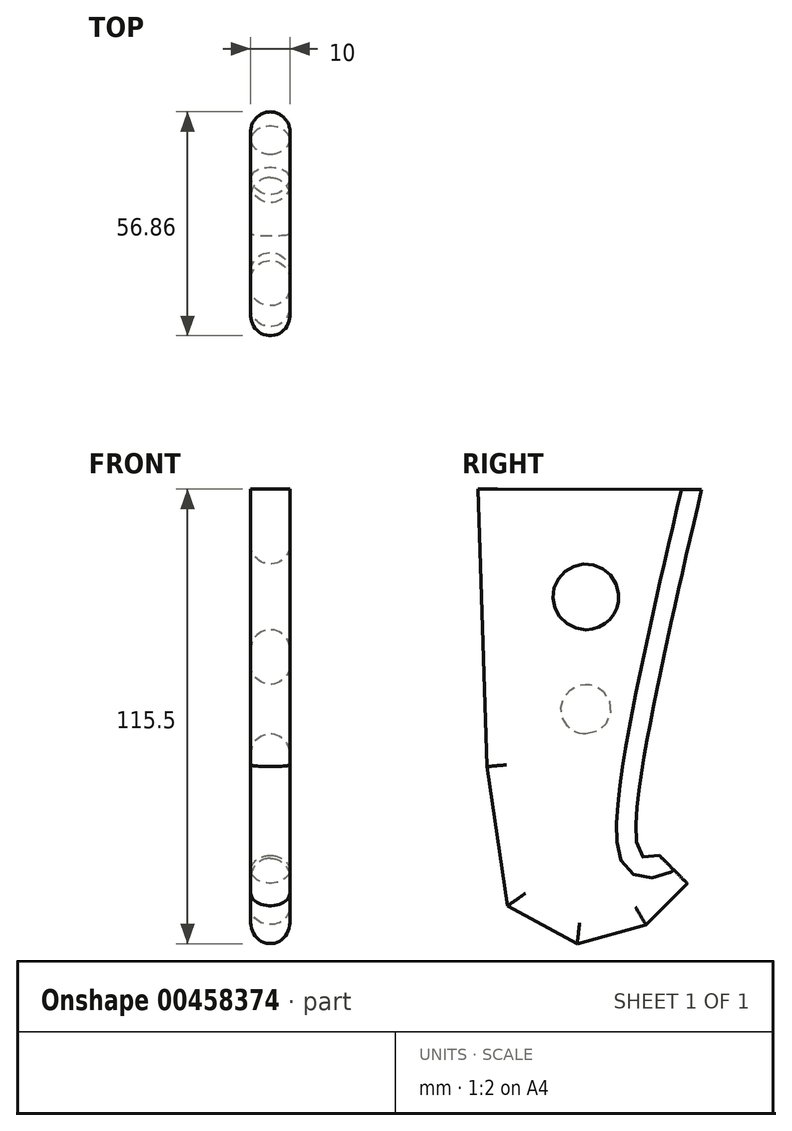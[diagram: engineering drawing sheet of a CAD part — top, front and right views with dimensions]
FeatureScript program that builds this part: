
annotation { "Feature Type Name" : "Feature", "Feature Type Description" : "" }
export const myFeature = defineFeature(function(context is Context, id is Id, definition is map)
    precondition{}
    {
        {
            var Q0;
            Q0=qCreatedBy(makeId("Top.planeOp"),FACE);
            var sketch = newSketch(context, id + "F0", { "sketchPlane" : qUnion([Q0])});
            skLineSegment(sketch, "E0.bottom", {"start": v(50, 50) * mm, "end": v(-50, 50) * mm});
            skLineSegment(sketch, "E0.top", {"start": v(50, -50) * mm, "end": v(-50, -50) * mm});
            skLineSegment(sketch, "E0.left", {"start": v(50, 50) * mm, "end": v(50, -50) * mm});
            skLineSegment(sketch, "E0.right", {"start": v(-50, 50) * mm, "end": v(-50, -50) * mm});
            skPoint(sketch, "E0.middle", {"position": v(0, 0) * mm});
            skSolve(sketch);
        }
        {
            var Q0;
            Q0=qCreatedBy(makeId("Right.planeOp"),FACE);
            var sketch = newSketch(context, id + "F1", { "sketchPlane" : qUnion([Q0])});
            skLineSegment(sketch, "E1", {"start": v(32.93, -92.93) * mm, "end": v(40, -100) * mm});
            skLineSegment(sketch, "E2", {"start": v(40, -100) * mm, "end": v(50, -100) * mm});
            skLineSegment(sketch, "E3", {"start": v(50, -100) * mm, "end": v(50, 0) * mm});
            skLineSegment(sketch, "E4", {"start": v(40, -100) * mm, "end": v(29.49, -110.51) * mm});
            skLineSegment(sketch, "E5", {"start": v(29.49, -110.51) * mm, "end": v(12.06, -115.35) * mm});
            skLineSegment(sketch, "E6", {"start": v(12.06, -115.35) * mm, "end": v(-5.63, -105.7) * mm});
            skLineSegment(sketch, "E7", {"start": v(-5.63, -105.7) * mm, "end": v(-10.9, -70.34) * mm});
            skLineSegment(sketch, "E8", {"start": v(-10.9, -70.34) * mm, "end": v(-13.2, 0.15) * mm});
            skFitSpline(sketch, "E9", {"points": [v(32.93, -92.93) * mm, v(28.21, -92.93) * mm, v(43.66, 0.05) * mm], "startDerivative": vector(-29.89, -10.4) * mm, "endDerivative": vector(37.17, 160.27) * mm});
            skLineSegment(sketch, "E10", {"start": v(43.66, 0.05) * mm, "end": v(-13.2, 0.15) * mm});
            skCircle(sketch, "E11", {"center": v(14.25, -27.21) * mm, "radius": 8.35 * mm});
            skCircle(sketch, "E12", {"center": v(14.25, -55.76) * mm, "radius": 6.33 * mm});
            skSolve(sketch);
        }
        {
            var Q0;
            Q0=makeQuery(id+"F1.imprint","IMPRINT",FACE,{"disambiguationData":[TD([[makeQuery(id+"F1.imprint","IMPRINT",EDGE,{"derivedFrom":sQuery(id+"F1.wireOp",EDGE,"E1")}),-1.0]])]});
            extrude(context, id + "F2", {"entities" : qUnion([Q0]), "endBound" : BoundingType.SYMMETRIC, "depth" : 10 * mm});
        }
        {
            var Q0;
            Q0=makeQuery(id+"F2.opExtrude","CAP_EDGE",EDGE,{"disambiguationData":[OSD([sQuery(id+"F1.wireOp",EDGE,"E4")])],"isStart":false});
            var Q1;
            Q1=makeQuery(id+"F2.opExtrude","CAP_EDGE",EDGE,{"disambiguationData":[OSD([sQuery(id+"F1.wireOp",EDGE,"E5")])],"isStart":false});
            var Q2;
            Q2=makeQuery(id+"F2.opExtrude","CAP_EDGE",EDGE,{"disambiguationData":[OSD([sQuery(id+"F1.wireOp",EDGE,"E6")])],"isStart":false});
            var Q3;
            Q3=makeQuery(id+"F2.opExtrude","CAP_EDGE",EDGE,{"disambiguationData":[OSD([sQuery(id+"F1.wireOp",EDGE,"E7")])],"isStart":false});
            var Q4;
            Q4=makeQuery(id+"F2.opExtrude","CAP_EDGE",EDGE,{"disambiguationData":[OSD([sQuery(id+"F1.wireOp",EDGE,"E8")])],"isStart":false});
            var Q5;
            Q5=makeQuery(id+"F2.opExtrude","CAP_EDGE",EDGE,{"disambiguationData":[OSD([sQuery(id+"F1.wireOp",EDGE,"E11")])],"isStart":false});
            var Q6;
            Q6=makeQuery(id+"F2.opExtrude","CAP_EDGE",EDGE,{"disambiguationData":[OSD([sQuery(id+"F1.wireOp",EDGE,"E12")])],"isStart":false});
            var Q7;
            Q7=makeQuery(id+"F2.opExtrude","CAP_EDGE",EDGE,{"disambiguationData":[OSD([sQuery(id+"F1.wireOp",EDGE,"E9")])],"isStart":true});
            var Q8;
            Q8=makeQuery(id+"F2.opExtrude","CAP_EDGE",EDGE,{"disambiguationData":[OSD([sQuery(id+"F1.wireOp",EDGE,"E4")])],"isStart":true});
            var Q9;
            Q9=makeQuery(id+"F2.opExtrude","CAP_EDGE",EDGE,{"disambiguationData":[OSD([sQuery(id+"F1.wireOp",EDGE,"E5")])],"isStart":true});
            var Q10;
            Q10=makeQuery(id+"F2.opExtrude","CAP_EDGE",EDGE,{"disambiguationData":[OSD([sQuery(id+"F1.wireOp",EDGE,"E6")])],"isStart":true});
            var Q11;
            Q11=makeQuery(id+"F2.opExtrude","CAP_EDGE",EDGE,{"disambiguationData":[OSD([sQuery(id+"F1.wireOp",EDGE,"E7")])],"isStart":true});
            var Q12;
            Q12=makeQuery(id+"F2.opExtrude","CAP_EDGE",EDGE,{"disambiguationData":[OSD([sQuery(id+"F1.wireOp",EDGE,"E8")])],"isStart":true});
            var Q13;
            Q13=makeQuery(id+"F2.opExtrude","CAP_EDGE",EDGE,{"disambiguationData":[OSD([sQuery(id+"F1.wireOp",EDGE,"E12")])],"isStart":true});
            var Q14;
            Q14=makeQuery(id+"F2.opExtrude","CAP_EDGE",EDGE,{"disambiguationData":[OSD([sQuery(id+"F1.wireOp",EDGE,"E11")])],"isStart":true});
            var Q15;
            Q15=makeQuery(id+"F2.opExtrude","CAP_EDGE",EDGE,{"disambiguationData":[OSD([sQuery(id+"F1.wireOp",EDGE,"E9")])],"isStart":false});
            fillet(context, id + "F3", {"entities" : qUnion([Q0, Q1, Q2, Q3, Q4, Q5, Q6, Q7, Q8, Q9, Q10, Q11, Q12, Q13, Q14, Q15]), "radius" : 5 * mm, "tangentPropagation" : true, "allowEdgeOverflow" : false});
        }
    });
